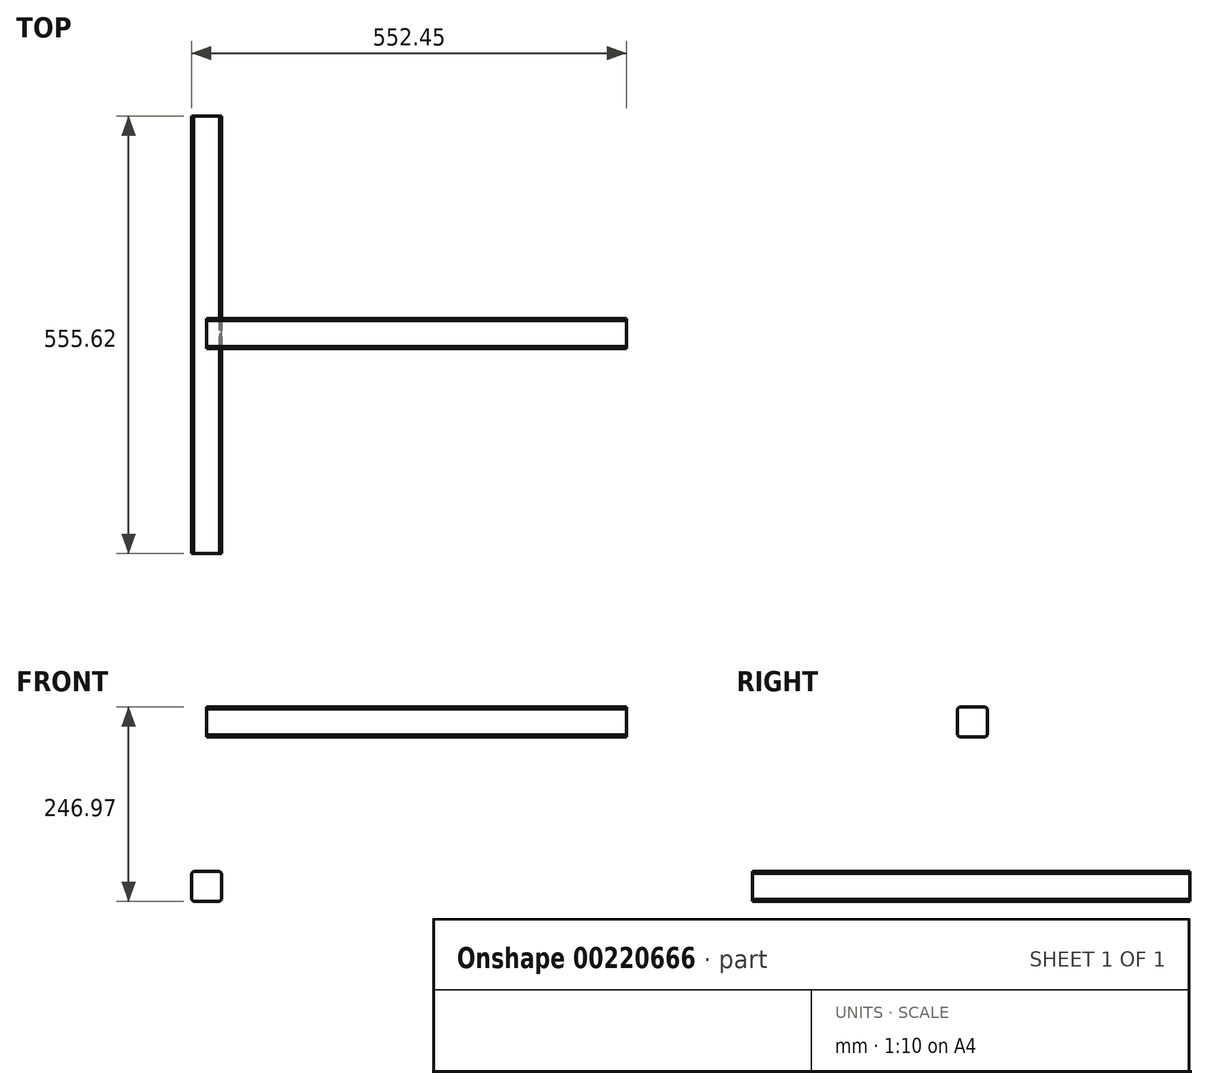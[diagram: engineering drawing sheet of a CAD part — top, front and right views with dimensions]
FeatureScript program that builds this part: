
annotation { "Feature Type Name" : "Feature", "Feature Type Description" : "" }
export const myFeature = defineFeature(function(context is Context, id is Id, definition is map)
    precondition{}
    {
        {
            var Q0;
            Q0=qCreatedBy(makeId("Front.planeOp"),FACE);
            var sketch = newSketch(context, id + "F0", { "sketchPlane" : qUnion([Q0])});
            skLineSegment(sketch, "E0.bottom", {"start": v(19.05, -19.05) * mm, "end": v(-19.05, -19.05) * mm});
            skLineSegment(sketch, "E0.top", {"start": v(19.05, 19.05) * mm, "end": v(-19.05, 19.05) * mm});
            skLineSegment(sketch, "E0.left", {"start": v(19.05, -19.05) * mm, "end": v(19.05, 19.05) * mm});
            skLineSegment(sketch, "E0.right", {"start": v(-19.05, -19.05) * mm, "end": v(-19.05, 19.05) * mm});
            skPoint(sketch, "E0.middle", {"position": v(0, 0) * mm});
            skSolve(sketch);
        }
        {
            var Q0;
            Q0 = qSketchRegion(id + "F0", true);
            extrude(context, id + "F1", {"entities" : qUnion([Q0]), "endBound" : BoundingType.SYMMETRIC, "depth" : 555.62 * mm});
        }
        {
            var Q0;
            Q0=makeQuery(id+"F1.opExtrude","SWEPT_EDGE",EDGE,{"disambiguationData":[OSD([sQuery(id+"F0.wireOp",EDGE,"E0.top"),sQuery(id+"F0.wireOp",EDGE,"E0.right")])]});
            var Q1;
            Q1=makeQuery(id+"F1.opExtrude","SWEPT_EDGE",EDGE,{"disambiguationData":[OSD([sQuery(id+"F0.wireOp",EDGE,"E0.top"),sQuery(id+"F0.wireOp",EDGE,"E0.left")])]});
            var Q2;
            Q2=makeQuery(id+"F1.opExtrude","SWEPT_EDGE",EDGE,{"disambiguationData":[OSD([sQuery(id+"F0.wireOp",EDGE,"E0.bottom"),sQuery(id+"F0.wireOp",EDGE,"E0.left")])]});
            var Q3;
            Q3=makeQuery(id+"F1.opExtrude","SWEPT_EDGE",EDGE,{"disambiguationData":[OSD([sQuery(id+"F0.wireOp",EDGE,"E0.bottom"),sQuery(id+"F0.wireOp",EDGE,"E0.right")])]});
            chamfer(context, id + "F2", {"entities" : qUnion([Q0, Q1, Q2, Q3]), "width" : 2.54 * mm, "tangentPropagation" : true});
        }
        {
            var Q0;
            Q0=qCreatedBy(makeId("Right.planeOp"),FACE);
            var sketch = newSketch(context, id + "F3", { "sketchPlane" : qUnion([Q0])});
            skLineSegment(sketch, "E1.bottom", {"start": v(-17.41, 189.82) * mm, "end": v(20.69, 189.82) * mm});
            skLineSegment(sketch, "E1.top", {"start": v(-17.41, 227.92) * mm, "end": v(20.69, 227.92) * mm});
            skLineSegment(sketch, "E1.left", {"start": v(-17.41, 189.82) * mm, "end": v(-17.41, 227.92) * mm});
            skLineSegment(sketch, "E1.right", {"start": v(20.69, 189.82) * mm, "end": v(20.69, 227.92) * mm});
            skSolve(sketch);
        }
        {
            var Q0;
            Q0 = qSketchRegion(id + "F3", true);
            extrude(context, id + "F4", {"entities" : qUnion([Q0]), "depth" : 533.4 * mm});
        }
        {
            var Q0;
            Q0=makeQuery(id+"F4.opExtrude","SWEPT_EDGE",EDGE,{"disambiguationData":[OSD([sQuery(id+"F3.wireOp",EDGE,"E1.bottom"),sQuery(id+"F3.wireOp",EDGE,"E1.left")])]});
            var Q1;
            Q1=makeQuery(id+"F4.opExtrude","SWEPT_EDGE",EDGE,{"disambiguationData":[OSD([sQuery(id+"F3.wireOp",EDGE,"E1.bottom"),sQuery(id+"F3.wireOp",EDGE,"E1.right")])]});
            var Q2;
            Q2=makeQuery(id+"F4.opExtrude","SWEPT_EDGE",EDGE,{"disambiguationData":[OSD([sQuery(id+"F3.wireOp",EDGE,"E1.top"),sQuery(id+"F3.wireOp",EDGE,"E1.right")])]});
            var Q3;
            Q3=makeQuery(id+"F4.opExtrude","SWEPT_EDGE",EDGE,{"disambiguationData":[OSD([sQuery(id+"F3.wireOp",EDGE,"E1.top"),sQuery(id+"F3.wireOp",EDGE,"E1.left")])]});
            chamfer(context, id + "F5", {"entities" : qUnion([Q0, Q1, Q2, Q3]), "width" : 2.54 * mm, "tangentPropagation" : true});
        }
        {
            var Q0;
            Q0=makeQuery(id+"F4.opExtrude","SWEPT_BODY",BODY,{"disambiguationData":[OSD([sQuery(id+"F3.wireOp",EDGE,"E1.bottom"),sQuery(id+"F3.wireOp",EDGE,"E1.top"),sQuery(id+"F3.wireOp",EDGE,"E1.left"),sQuery(id+"F3.wireOp",EDGE,"E1.right")])]});
            transform(context, id + "F6", {"entities" : qUnion([Q0]), "transformType" : TransformType.TRANSLATION_3D, "dx" : 25.4 * mm, "dy" : 0 * mm, "dz" : 0 * mm, "makeCopy" : true});
        }
        {
            var Q0;
            Q0=makeQuery(id+"F6.opPattern","COPY",BODY,{"derivedFrom":makeQuery(id+"F4.opExtrude","SWEPT_BODY",BODY,{"disambiguationData":[OSD([sQuery(id+"F3.wireOp",EDGE,"E1.bottom"),sQuery(id+"F3.wireOp",EDGE,"E1.top"),sQuery(id+"F3.wireOp",EDGE,"E1.left"),sQuery(id+"F3.wireOp",EDGE,"E1.right")])]}),"instanceName":"1"});
            deleteBodies(context, id + "F7", {"entities" : qUnion([Q0])});
        }
        {
            var Q0;
            Q0=makeQuery(id+"F4.opExtrude","SWEPT_BODY",BODY,{"disambiguationData":[OSD([sQuery(id+"F3.wireOp",EDGE,"E1.bottom"),sQuery(id+"F3.wireOp",EDGE,"E1.top"),sQuery(id+"F3.wireOp",EDGE,"E1.left"),sQuery(id+"F3.wireOp",EDGE,"E1.right")])]});
            transform(context, id + "F8", {"entities" : qUnion([Q0]), "transformType" : TransformType.TRANSLATION_3D, "dx" : 0 * mm, "dy" : 0 * mm, "dz" : 0 * mm, "makeCopy" : true});
        }
        {
            var Q0;
            Q0=makeQuery(id+"F8.opPattern","COPY",BODY,{"derivedFrom":makeQuery(id+"F4.opExtrude","SWEPT_BODY",BODY,{"disambiguationData":[OSD([sQuery(id+"F3.wireOp",EDGE,"E1.bottom"),sQuery(id+"F3.wireOp",EDGE,"E1.top"),sQuery(id+"F3.wireOp",EDGE,"E1.left"),sQuery(id+"F3.wireOp",EDGE,"E1.right")])]}),"instanceName":"1"});
            deleteBodies(context, id + "F9", {"entities" : qUnion([Q0])});
        }
    });
